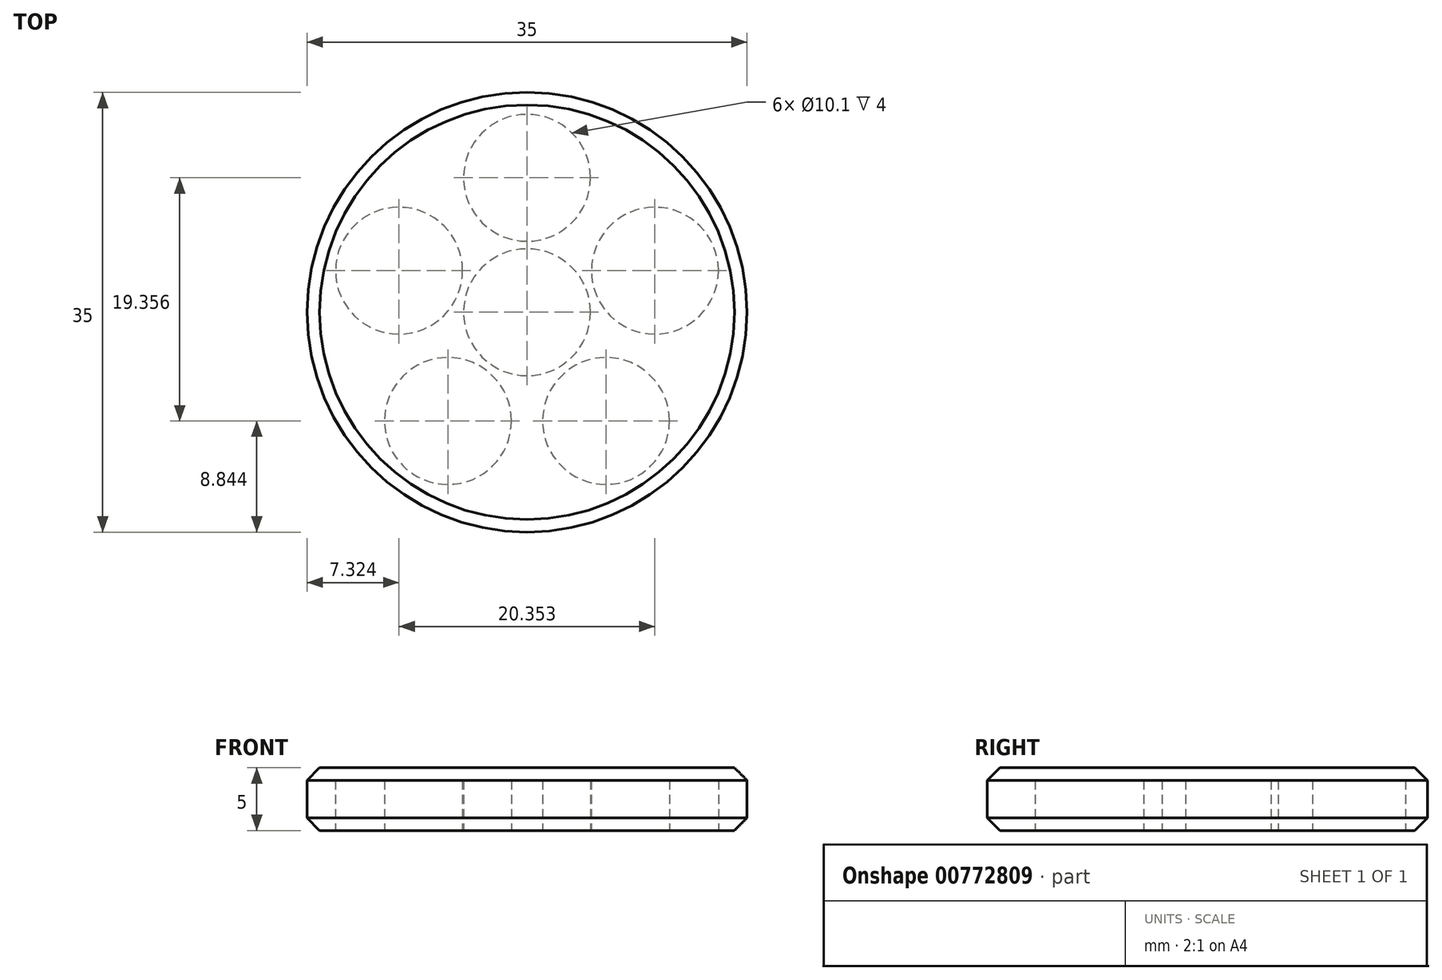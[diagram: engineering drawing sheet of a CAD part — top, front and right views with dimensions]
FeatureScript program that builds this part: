
annotation { "Feature Type Name" : "Feature", "Feature Type Description" : "" }
export const myFeature = defineFeature(function(context is Context, id is Id, definition is map)
    precondition{}
    {
        {
            var Q0;
            Q0=qCreatedBy(makeId("Top.planeOp"),FACE);
            var sketch = newSketch(context, id + "F0", { "sketchPlane" : qUnion([Q0])});
            skCircle(sketch, "E0", {"center": v(0, 0) * mm, "radius": 5.05 * mm});
            skLineSegment(sketch, "E1", {"start": v(0, 0) * mm, "end": v(0, 10.7) * mm, "construction": true});
            skCircle(sketch, "E2", {"center": v(0, 10.7) * mm, "radius": 5.05 * mm});
            skCircle(sketch, "E3.1.0", {"center": v(-10.18, 3.3) * mm, "radius": 5.05 * mm});
            skCircle(sketch, "E3.2.0", {"center": v(-6.29, -8.66) * mm, "radius": 5.05 * mm});
            skCircle(sketch, "E3.3.0", {"center": v(6.29, -8.66) * mm, "radius": 5.05 * mm});
            skCircle(sketch, "E3.4.0", {"center": v(10.18, 3.3) * mm, "radius": 5.05 * mm});
            skCircle(sketch, "E4", {"center": v(0, 0) * mm, "radius": 17.5 * mm});
            skSolve(sketch);
        }
        {
            var Q0;
            Q0 = qSketchRegion(id + "F0", true);
            extrude(context, id + "F1", {"entities" : qUnion([Q0]), "depth" : 4 * mm, "offsetDistance" : 25 * mm});
        }
        {
            var Q0;
            Q0=makeQuery(id+"F1.opExtrude","CAP_FACE",FACE,{"disambiguationData":[OSD([sQuery(id+"F0.wireOp",EDGE,"E0"),sQuery(id+"F0.wireOp",EDGE,"E2"),sQuery(id+"F0.wireOp",EDGE,"E3.1.0"),sQuery(id+"F0.wireOp",EDGE,"E3.2.0"),sQuery(id+"F0.wireOp",EDGE,"E3.3.0"),sQuery(id+"F0.wireOp",EDGE,"E3.4.0"),sQuery(id+"F0.wireOp",EDGE,"E4")])],"isStart":false});
            var sketch = newSketch(context, id + "F2", { "sketchPlane" : qUnion([Q0])});
            skCircle(sketch, "E5.0", {"center": v(0, 0) * mm, "radius": 17.5 * mm});
            skSolve(sketch);
        }
        {
            var Q0;
            Q0 = qSketchRegion(id + "F2", true);
            extrude(context, id + "F3", {"entities" : qUnion([Q0]), "operationType" : NewBodyOperationType.ADD, "depth" : 1 * mm, "offsetDistance" : 25 * mm});
        }
        {
            var Q0;
            Q0=makeQuery(id+"F1.opExtrude","CAP_EDGE",EDGE,{"disambiguationData":[OSD([sQuery(id+"F0.wireOp",EDGE,"E4")])],"isStart":true});
            chamfer(context, id + "F4", {"entities" : qUnion([Q0]), "width" : 1 * mm, "tangentPropagation" : true});
        }
        {
            var Q0;
            Q0=makeQuery(id+"F3.opExtrude","CAP_EDGE",EDGE,{"disambiguationData":[OSD([sQuery(id+"F2.wireOp",EDGE,"E5.0")])],"isStart":false});
            chamfer(context, id + "F5", {"entities" : qUnion([Q0]), "width" : 1 * mm, "tangentPropagation" : true});
        }
    });
